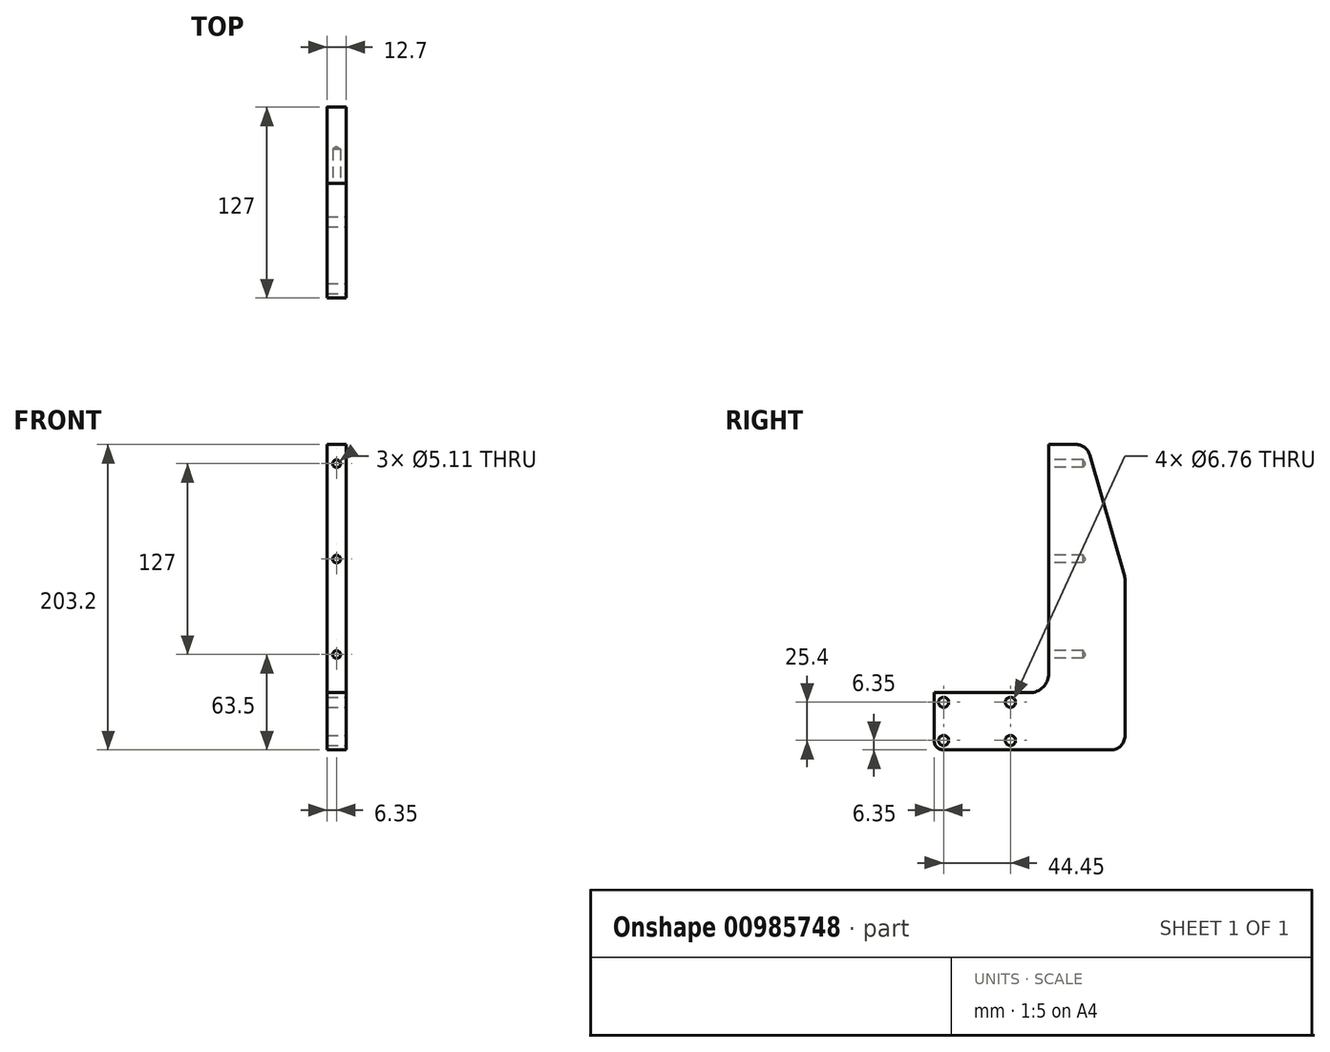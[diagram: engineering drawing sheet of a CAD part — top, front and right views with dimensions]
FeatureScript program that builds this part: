
annotation { "Feature Type Name" : "Feature", "Feature Type Description" : "" }
export const myFeature = defineFeature(function(context is Context, id is Id, definition is map)
    precondition{}
    {
        {
            var Q0;
            Q0=qCreatedBy(makeId("Right.planeOp"),FACE);
            var sketch = newSketch(context, id + "F0", { "sketchPlane" : qUnion([Q0])});
            skLineSegment(sketch, "E0.bottom", {"start": v(0, 0) * mm, "end": v(127, 0) * mm});
            skLineSegment(sketch, "E0.top", {"start": v(0, 203.2) * mm, "end": v(127, 203.2) * mm});
            skLineSegment(sketch, "E0.left", {"start": v(0, 0) * mm, "end": v(0, 203.2) * mm});
            skLineSegment(sketch, "E0.right", {"start": v(127, 0) * mm, "end": v(127, 203.2) * mm});
            skSolve(sketch);
        }
        {
            var Q0;
            Q0 = qSketchRegion(id + "F0", true);
            extrude(context, id + "F1", {"entities" : qUnion([Q0]), "depth" : 12.7 * mm, "offsetDistance" : 25.4 * mm});
        }
        {
            var Q0;
            Q0=makeQuery(id+"F1.opExtrude","CAP_FACE",FACE,{"disambiguationData":[OSD([sQuery(id+"F0.wireOp",EDGE,"E0.bottom"),sQuery(id+"F0.wireOp",EDGE,"E0.top"),sQuery(id+"F0.wireOp",EDGE,"E0.left"),sQuery(id+"F0.wireOp",EDGE,"E0.right")])],"isStart":false});
            var sketch = newSketch(context, id + "F2", { "sketchPlane" : qUnion([Q0])});
            skLineSegment(sketch, "E1", {"start": v(6.35, 31.75) * mm, "end": v(50.8, 31.75) * mm, "construction": true});
            skLineSegment(sketch, "E2", {"start": v(50.8, 31.75) * mm, "end": v(50.8, 6.35) * mm, "construction": true});
            skLineSegment(sketch, "E3", {"start": v(50.8, 6.35) * mm, "end": v(6.35, 6.35) * mm, "construction": true});
            skLineSegment(sketch, "E4", {"start": v(6.35, 6.35) * mm, "end": v(6.35, 31.75) * mm, "construction": true});
            skPoint(sketch, "E5", {"position": v(6.35, 31.75) * mm});
            skPoint(sketch, "E6", {"position": v(50.8, 31.75) * mm});
            skPoint(sketch, "E7", {"position": v(50.8, 6.35) * mm});
            skPoint(sketch, "E8", {"position": v(6.35, 6.35) * mm});
            skSolve(sketch);
        }
        {
            var Q0;
            Q0=sQuery(id+"F2.wireOp",VERTEX,"E5");
            var Q1;
            Q1=sQuery(id+"F2.wireOp",VERTEX,"E6");
            var Q2;
            Q2=sQuery(id+"F2.wireOp",VERTEX,"E7");
            var Q3;
            Q3=sQuery(id+"F2.wireOp",VERTEX,"E8");
            var Q4;
            Q4=makeQuery(id+"F1.opExtrude","SWEPT_BODY",BODY,{"disambiguationData":[OSD([sQuery(id+"F0.wireOp",EDGE,"E0.bottom"),sQuery(id+"F0.wireOp",EDGE,"E0.top"),sQuery(id+"F0.wireOp",EDGE,"E0.left"),sQuery(id+"F0.wireOp",EDGE,"E0.right")])]});
            hole(context, id + "F3", {"style" : HoleStyle.SIMPLE, "endStyle" : HoleEndStyle.THROUGH, "standardTappedOrClearance" : lookupTablePath({ "fit" : "Free", "standard" : "ANSI", "size" : "1/4", "type" : "Clearance" }), "standardBlindInLast" : lookupTablePath({ "fit" : "Free", "standard" : "ANSI", "engagement" : "75%", "pitch" : "20 tpi", "size" : "1/4", "type" : "Clearance & tapped" }), "holeDiameter" : 6.76 * mm, "majorDiameter" : 7.94 * mm, "isTappedThrough" : true, "tappedDepth" : 19.05 * mm, "tapClearance" : 3, "startFromSketch" : true, "locations" : qUnion([Q0, Q1, Q2, Q3]), "scope" : qUnion([Q4])});
        }
        {
            var Q0;
            Q0=makeQuery(id+"F1.opExtrude","CAP_FACE",FACE,{"disambiguationData":[OSD([sQuery(id+"F0.wireOp",EDGE,"E0.bottom"),sQuery(id+"F0.wireOp",EDGE,"E0.top"),sQuery(id+"F0.wireOp",EDGE,"E0.left"),sQuery(id+"F0.wireOp",EDGE,"E0.right")])],"isStart":false});
            var sketch = newSketch(context, id + "F4", { "sketchPlane" : qUnion([Q0])});
            skLineSegment(sketch, "E9", {"start": v(0, 203.2) * mm, "end": v(0, 38.1) * mm});
            skLineSegment(sketch, "E10", {"start": v(0, 38.1) * mm, "end": v(76.2, 38.1) * mm});
            skLineSegment(sketch, "E11", {"start": v(76.2, 38.1) * mm, "end": v(76.2, 203.2) * mm});
            skLineSegment(sketch, "E12", {"start": v(76.2, 203.2) * mm, "end": v(0, 203.2) * mm});
            skSolve(sketch);
        }
        {
            var Q0;
            Q0 = qSketchRegion(id + "F4", true);
            extrude(context, id + "F5", {"entities" : qUnion([Q0]), "operationType" : NewBodyOperationType.REMOVE, "endBound" : BoundingType.UP_TO_NEXT, "oppositeDirection" : true, "depth" : 25.4 * mm, "offsetDistance" : 25.4 * mm});
        }
        {
            var Q0;
            Q0=makeQuery(id+"F5.boolean.opBoolean","COPY",FACE,{"derivedFrom":makeQuery(id+"F5.opExtrude","SWEPT_FACE",FACE,{"disambiguationData":[OSD([sQuery(id+"F4.wireOp",EDGE,"E11")])]})});
            var sketch = newSketch(context, id + "F6", { "sketchPlane" : qUnion([Q0])});
            skLineSegment(sketch, "E13", {"start": v(6.35, 203.2) * mm, "end": v(6.35, 190.5) * mm, "construction": true});
            skLineSegment(sketch, "E14", {"start": v(6.35, 190.5) * mm, "end": v(6.35, 63.5) * mm, "construction": true});
            skPoint(sketch, "E15", {"position": v(6.35, 190.5) * mm});
            skPoint(sketch, "E16", {"position": v(6.35, 63.5) * mm});
            skPoint(sketch, "E17", {"position": v(6.35, 127) * mm});
            skSolve(sketch);
        }
        {
            var Q0;
            Q0=makeQuery(id+"F5.boolean.opBoolean","COPY",EDGE,{"derivedFrom":makeQuery(id+"F5.opExtrude","SWEPT_EDGE",EDGE,{"disambiguationData":[OSD([sQuery(id+"F4.wireOp",EDGE,"E10"),sQuery(id+"F4.wireOp",EDGE,"E11")])]})});
            fillet(context, id + "F7", {"entities" : qUnion([Q0]), "tangentPropagation" : true, "radius" : 12.7 * mm, "defaultsChanged" : true, "vertexSettings" : [], "allowEdgeOverflow" : false});
        }
        {
            var Q0;
            Q0=sQuery(id+"F6.wireOp",VERTEX,"E15");
            var Q1;
            Q1=sQuery(id+"F6.wireOp",VERTEX,"E17");
            var Q2;
            Q2=sQuery(id+"F6.wireOp",VERTEX,"E16");
            var Q3;
            Q3=makeQuery(id+"F1.opExtrude","SWEPT_BODY",BODY,{"disambiguationData":[OSD([sQuery(id+"F0.wireOp",EDGE,"E0.bottom"),sQuery(id+"F0.wireOp",EDGE,"E0.top"),sQuery(id+"F0.wireOp",EDGE,"E0.left"),sQuery(id+"F0.wireOp",EDGE,"E0.right")])]});
            hole(context, id + "F8", {"style" : HoleStyle.SIMPLE, "endStyle" : HoleEndStyle.BLIND, "standardTappedOrClearance" : lookupTablePath({ "standard" : "ANSI", "engagement" : "75%", "pitch" : "20 tpi", "size" : "1/4", "type" : "Tapped" }), "standardBlindInLast" : lookupTablePath({ "standard" : "ANSI", "fit" : "Free", "engagement" : "75%", "pitch" : "20 tpi", "size" : "1/4", "type" : "Clearance & tapped" }), "holeDiameter" : 5.1 * mm, "majorDiameter" : 6.35 * mm, "showTappedDepth" : true, "holeDepth" : 22.86 * mm, "isTappedThrough" : true, "tappedDepth" : 19.05 * mm, "tapClearance" : 3, "startFromSketch" : true, "locations" : qUnion([Q0, Q1, Q2]), "scope" : qUnion([Q3])});
        }
        {
            var Q0;
            Q0=makeQuery(id+"F1.opExtrude","SWEPT_EDGE",EDGE,{"disambiguationData":[OSD([sQuery(id+"F0.wireOp",EDGE,"E0.top"),sQuery(id+"F0.wireOp",EDGE,"E0.right")])]});
            chamfer(context, id + "F9", {"entities" : qUnion([Q0]), "chamferType" : ChamferType.TWO_OFFSETS, "width1" : 25.4 * mm, "oppositeDirection" : false, "width2" : 88.9 * mm});
        }
        {
            var Q0;
            Q0=makeQuery(id+"F1.opExtrude","SWEPT_EDGE",EDGE,{"disambiguationData":[OSD([sQuery(id+"F0.wireOp",EDGE,"E0.bottom"),sQuery(id+"F0.wireOp",EDGE,"E0.right")])]});
            var Q1;
            {var subQ0=sQuery(id+"F0.wireOp",EDGE,"E0.top");Q1=makeQuery(id+"F9.opChamfer","BLEND_EDGE",EDGE,{"blendedFrom":[makeQuery(id+"F1.opExtrude","SWEPT_EDGE",EDGE,{"disambiguationData":[OSD([subQ0,sQuery(id+"F0.wireOp",EDGE,"E0.right")])]}),makeQuery(id+"F1.opExtrude","SWEPT_FACE",FACE,{"disambiguationData":[OSD([subQ0])]})],"blendedInto":[makeQuery(id+"F1.opExtrude","SWEPT_FACE",FACE,{"disambiguationData":[OSD([subQ0])]})]});}
            var Q2;
            {var subQ0=sQuery(id+"F0.wireOp",EDGE,"E0.right");Q2=makeQuery(id+"F9.opChamfer","BLEND_EDGE",EDGE,{"blendedFrom":[makeQuery(id+"F1.opExtrude","SWEPT_EDGE",EDGE,{"disambiguationData":[OSD([sQuery(id+"F0.wireOp",EDGE,"E0.top"),subQ0])]}),makeQuery(id+"F1.opExtrude","SWEPT_FACE",FACE,{"disambiguationData":[OSD([subQ0])]})],"blendedInto":[makeQuery(id+"F1.opExtrude","SWEPT_FACE",FACE,{"disambiguationData":[OSD([subQ0])]})]});}
            fillet(context, id + "F10", {"entities" : qUnion([Q0, Q1, Q2]), "tangentPropagation" : true, "radius" : 9.52 * mm, "defaultsChanged" : false, "vertexSettings" : [], "allowEdgeOverflow" : false});
        }
        {
            var Q0;
            Q0=makeQuery(id+"F5.boolean.opBoolean","COPY",EDGE,{"derivedFrom":makeQuery(id+"F5.opExtrude","SWEPT_EDGE",EDGE,{"disambiguationData":[OSD([sQuery(id+"F0.wireOp",EDGE,"E0.left"),sQuery(id+"F4.wireOp",EDGE,"E9"),sQuery(id+"F4.wireOp",EDGE,"E10")])]})});
            var Q1;
            Q1=makeQuery(id+"F1.opExtrude","SWEPT_EDGE",EDGE,{"disambiguationData":[OSD([sQuery(id+"F0.wireOp",EDGE,"E0.bottom"),sQuery(id+"F0.wireOp",EDGE,"E0.left")])]});
            fillet(context, id + "F11", {"entities" : qUnion([Q0, Q1]), "tangentPropagation" : true, "radius" : 6.35 * mm, "defaultsChanged" : false, "vertexSettings" : [], "allowEdgeOverflow" : false});
        }
    });
